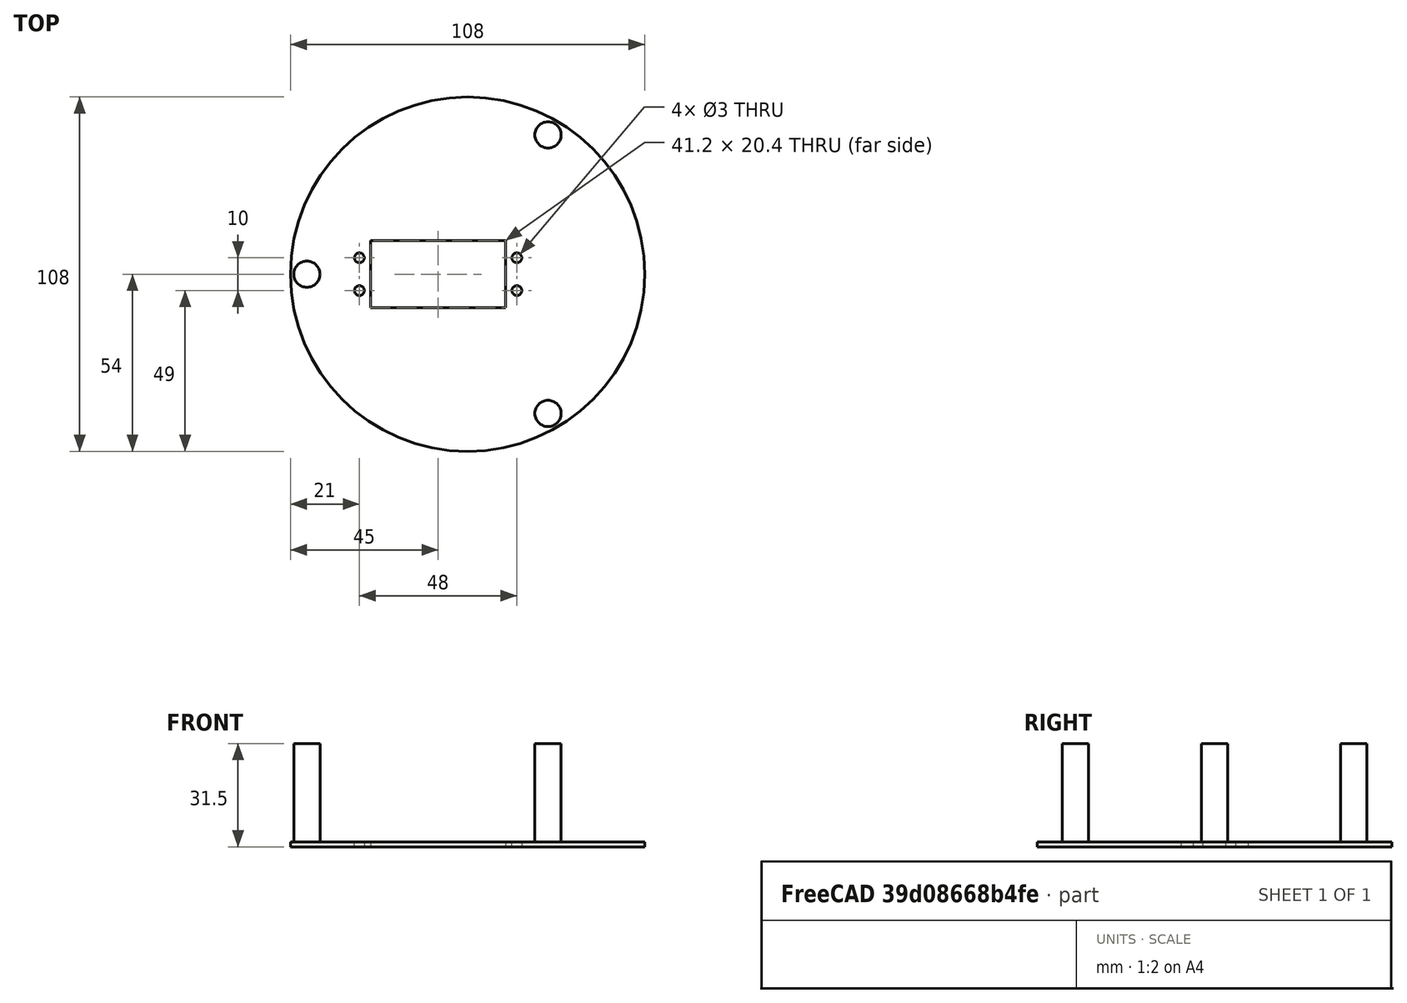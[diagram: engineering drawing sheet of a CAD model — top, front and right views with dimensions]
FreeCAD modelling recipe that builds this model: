
FCSTD DOCUMENT  (FreeCAD 0.20RUnknown)
Label: camera_socket
License: All rights reserved
LicenseURL: http://en.wikipedia.org/wiki/All_rights_reserved
objects: Sketcher::SketchObject×3, PartDesign::Pad×2, PartDesign::Pocket×1, PartDesign::Body×1, Mesh::Feature×1
note: 10 computed .brp shape members not serialized (recipe doc carries the construction recipe); baked Part::Feature solids carry a one-line shape summary decoded from their .brp

FEATURE [Sketcher::SketchObject] Sketch
  FullyConstrained = true
  MapMode = 5
  Support = -> [XY_Plane]
  sketch-geometry (1):
    g0: Circle CenterX=0 CenterY=0 CenterZ=0 NormalX=0 NormalY=0 NormalZ=1 AngleXU=0 Radius=54
  constraints (2):
    c: Coincident(g0,g-1)
    c: Diameter(g0) = 108
FEATURE [PartDesign::Pad] Pad
  Direction = (0,0,1)
  Length = 1.5
  Length2 = 10
  Profile = -> Sketch
  ReferenceAxis = -> Sketch [N_Axis]
  Type = 0
FEATURE [Sketcher::SketchObject] Sketch001
  FullyConstrained = true
  MapMode = 5
  Placement = pos=(0,0,1.5) rot=(0,0,1;0rad)
  Support = -> [Pad]
  sketch-geometry (9):
    g0: LineSegment StartX=-29.6 StartY=10.2 StartZ=0 EndX=11.6 EndY=10.2 EndZ=0
    g1: LineSegment StartX=11.6 StartY=10.2 StartZ=0 EndX=11.6 EndY=-10.2 EndZ=0
    g2: LineSegment StartX=11.6 StartY=-10.2 StartZ=0 EndX=-29.6 EndY=-10.2 EndZ=0
    g3: LineSegment StartX=-29.6 StartY=-10.2 StartZ=0 EndX=-29.6 EndY=10.2 EndZ=0
    g4: Circle CenterX=-33 CenterY=5 CenterZ=0 NormalX=0 NormalY=0 NormalZ=1 AngleXU=0 Radius=1.5
    g5: Circle CenterX=-33 CenterY=-5 CenterZ=0 NormalX=0 NormalY=0 NormalZ=1 AngleXU=0 Radius=1.5
    g6: Circle CenterX=15 CenterY=5 CenterZ=0 NormalX=0 NormalY=0 NormalZ=1 AngleXU=0 Radius=1.5
    g7: Circle CenterX=15 CenterY=-5 CenterZ=0 NormalX=0 NormalY=0 NormalZ=1 AngleXU=0 Radius=1.5
    g8: GeomPoint X=-9 Y=4e-16 Z=0
  constraints (22):
    c: Coincident(g0,g1)
    c: Coincident(g1,g2)
    c: Coincident(g2,g3)
    c: Coincident(g3,g0)
    c: Horizontal(g0)
    c: Horizontal(g2)
    c: Vertical(g1)
    c: Distance(g0) = 41.2
    c: Distance(g1) = 20.4
    c: Symmetric(g0,g2,g-1)
    c: Diameter(g4) = 3
    c: Diameter(g5) = 3
    c: Diameter(g6) = 3
    c: Diameter(g7) = 3
    c: Symmetric(g0,g1,g8)
    c: Distance(g-1,g8) = 9
    c: Symmetric(g4,g5,g-1)
    c: Symmetric(g6,g7,g-1)
    c: Distance(g4,g6) = 48
    c: Horizontal(g6,g4)
    c: Distance(g6,g7) = 10
    c: DistanceX(g-2,g6) = 15
FEATURE [PartDesign::Pocket] Pocket
  BaseFeature = -> Pad
  Direction = (0,0,-1)
  Length = 15
  Length2 = 5
  Profile = -> Sketch001
  ReferenceAxis = -> Sketch001 [N_Axis]
  Type = 0
FEATURE [Sketcher::SketchObject] Sketch002
  FullyConstrained = true
  MapMode = 5
  Placement = pos=(0,0,1.5) rot=(0,0,1;0rad)
  Support = -> [Pocket]
  sketch-geometry (6):
    g0: Circle CenterX=-49 CenterY=0 CenterZ=0 NormalX=0 NormalY=0 NormalZ=1 AngleXU=0 Radius=4
    g1: Circle CenterX=24.5 CenterY=42.4352 CenterZ=0 NormalX=0 NormalY=0 NormalZ=1 AngleXU=0 Radius=4
    g2: Circle CenterX=24.5 CenterY=-42.4352 CenterZ=0 NormalX=0 NormalY=0 NormalZ=1 AngleXU=0 Radius=4
    g3: LineSegment StartX=24.5 StartY=-42.4352 StartZ=0 EndX=0 EndY=0 EndZ=0
    g4: LineSegment StartX=0 StartY=0 StartZ=0 EndX=24.5 EndY=42.4352 EndZ=0
    g5: LineSegment StartX=0 StartY=0 StartZ=0 EndX=-49 EndY=0 EndZ=0
  constraints (15):
    c: Diameter(g2) = 8
    c: Distance(g-1,g2) = 49
    c: Diameter(g1) = 8
    c: Diameter(g0) = 8
    c: Distance(g-1,g0) = 49
    c: Distance(g-1,g1) = 49
    c: Coincident(g3,g2)
    c: Coincident(g3,g-1)
    c: Coincident(g4,g3)
    c: Coincident(g4,g1)
    c: Coincident(g5,g3)
    c: Coincident(g5,g0)
    c: Angle(g4,g5) = 2.0944
    c: Angle(g3,g4) = 2.0944
    c: PointOnObject(g0,g-1)
FEATURE [PartDesign::Pad] Pad001
  BaseFeature = -> Pocket
  Direction = (0,0,1)
  Length = 30
  Length2 = 10
  Profile = -> Sketch002
  ReferenceAxis = -> Sketch002 [N_Axis]
  Type = 0
FEATURE [PartDesign::Body] Body
  Group = -> [Sketch,Pad,Sketch001,Pocket,Sketch002,Pad001]
  Origin = -> Origin
  Tip = -> Pad001
FEATURE [Mesh::Feature] Mesh  label="Body (Meshed)"
